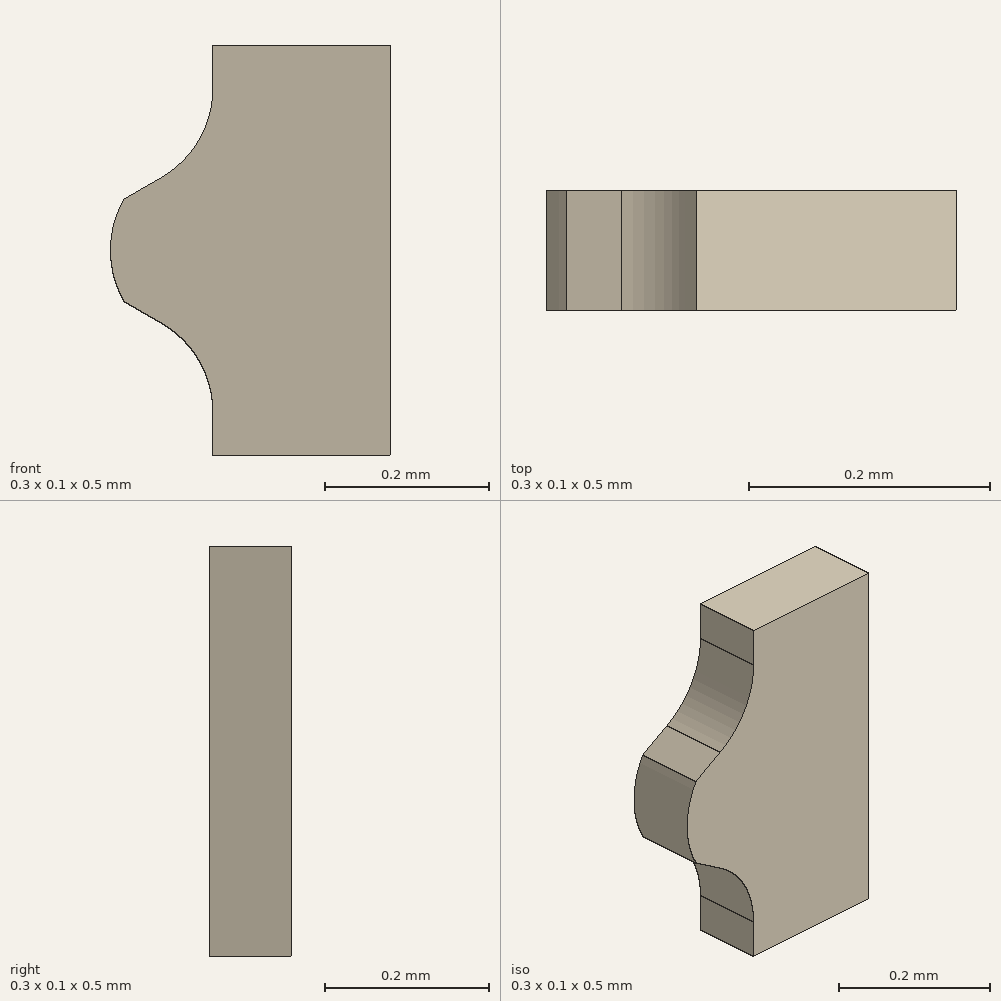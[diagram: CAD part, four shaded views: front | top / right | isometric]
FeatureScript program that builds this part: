
annotation { "Feature Type Name" : "Feature", "Feature Type Description" : "" }
export const myFeature = defineFeature(function(context is Context, id is Id, definition is map)
    precondition{}
    {
        {
            var Q0;
            Q0=qCreatedBy(makeId("Front.planeOp"),FACE);
            var sketch = newSketch(context, id + "F0", { "sketchPlane" : qUnion([Q0])});
            skLineSegment(sketch, "E0", {"start": v(0, 0) * mm, "end": v(0.1, 0.06) * mm, "construction": true});
            skLineSegment(sketch, "E1", {"start": v(0, 0) * mm, "end": v(0.1, -0.06) * mm, "construction": true});
            skLineSegment(sketch, "E2", {"start": v(0, 0) * mm, "end": v(0.43, 0) * mm, "construction": true});
            skLineSegment(sketch, "E3", {"start": v(0.43, 0.25) * mm, "end": v(0.43, -0.25) * mm});
            skLineSegment(sketch, "E4", {"start": v(0.22, 0.13) * mm, "end": v(0.22, -0.13) * mm, "construction": true});
            skLineSegment(sketch, "E5", {"start": v(0.1, 0.06) * mm, "end": v(0.1, -0.06) * mm, "construction": true});
            skArc(sketch, "E6", {"start": v(0.1, -0.06) * mm, "mid": v(0.1, 0) * mm, "end": v(0.1, 0.06) * mm});
            skLineSegment(sketch, "E7", {"start": v(0.1, -0.06) * mm, "end": v(0.15, -0.09) * mm});
            skLineSegment(sketch, "E8", {"start": v(0.1, 0.06) * mm, "end": v(0.15, 0.09) * mm});
            skLineSegment(sketch, "E9", {"start": v(0.43, -0.25) * mm, "end": v(0.22, -0.25) * mm});
            skLineSegment(sketch, "E10", {"start": v(0.43, 0.25) * mm, "end": v(0.22, 0.25) * mm});
            skLineSegment(sketch, "E11", {"start": v(0.22, 0.25) * mm, "end": v(0.22, 0.2) * mm});
            skLineSegment(sketch, "E12", {"start": v(0.22, 0.12) * mm, "end": v(0.22, -0.12) * mm, "construction": true});
            skLineSegment(sketch, "E13", {"start": v(0.22, -0.2) * mm, "end": v(0.22, -0.25) * mm});
            skLineSegment(sketch, "E14", {"start": v(0.22, 0.12) * mm, "end": v(0.43, 0.25) * mm, "construction": true});
            skLineSegment(sketch, "E15", {"start": v(0.22, -0.12) * mm, "end": v(0.43, -0.25) * mm, "construction": true});
            skPoint(sketch, "E16.visualSharp", {"position": v(0.22, 0.12) * mm});
            skArc(sketch, "E16.filletArc", {"start": v(0.15, 0.09) * mm, "mid": v(0.2, 0.13) * mm, "end": v(0.22, 0.2) * mm});
            skPoint(sketch, "E17.visualSharp", {"position": v(0.22, -0.12) * mm});
            skArc(sketch, "E17.filletArc", {"start": v(0.22, -0.2) * mm, "mid": v(0.2, -0.13) * mm, "end": v(0.15, -0.09) * mm});
            skSolve(sketch);
        }
        {
            var Q0;
            Q0=makeQuery(id+"F0.imprint","IMPRINT",FACE,{"disambiguationData":[TD([[makeQuery(id+"F0.imprint","IMPRINT",EDGE,{"derivedFrom":sQuery(id+"F0.wireOp",EDGE,"E3")}),-1.0]])]});
            extrude(context, id + "F1", {"entities" : qUnion([Q0]), "depth" : .1 * mm});
        }
    });
